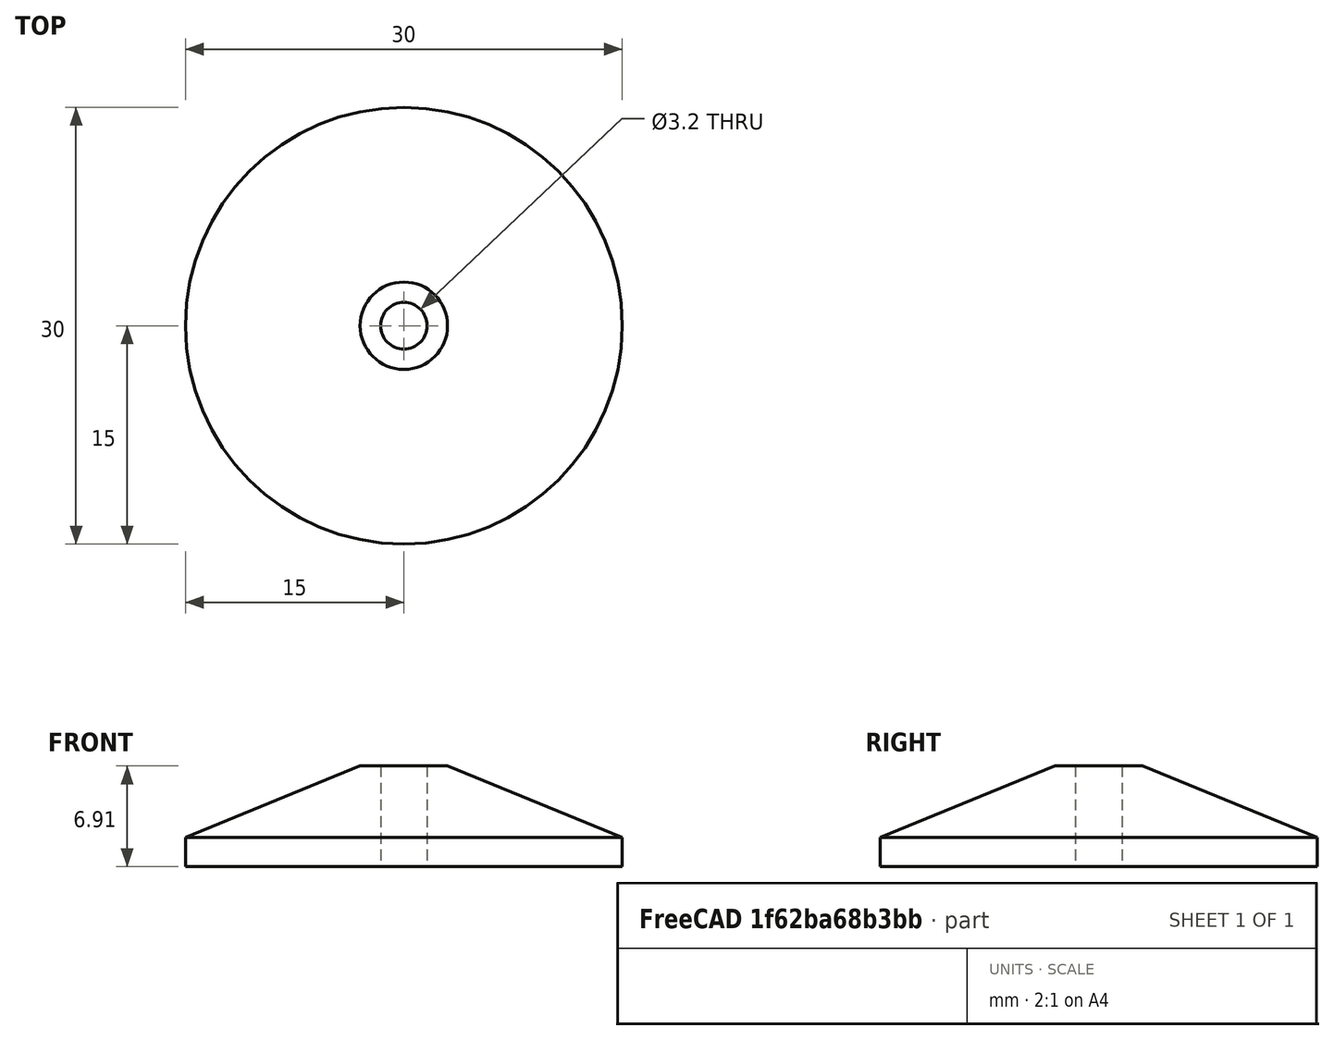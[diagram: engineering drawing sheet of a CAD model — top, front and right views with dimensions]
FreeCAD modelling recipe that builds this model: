
FCSTD DOCUMENT  (FreeCAD 0.21R33668 +26 (Git))
Label: BobbinSocket_Small_R_A2
License: All rights reserved
LicenseURL: http://en.wikipedia.org/wiki/All_rights_reserved
objects: Sketcher::SketchObject×1, PartDesign::Revolution×1, PartDesign::Body×1, App::Part×1
note: 4 computed .brp shape members not serialized (recipe doc carries the construction recipe); baked Part::Feature solids carry a one-line shape summary decoded from their .brp

FEATURE [Sketcher::SketchObject] Sketch002
  FullyConstrained = false
  MapMode = 5
  Placement = pos=(0,0,0) rot=(0.57735,0.57735,0.57735;2.0944rad)
  Support = -> [YZ_Plane001]
  sketch-geometry (5):
    g0: LineSegment StartX=1.6 StartY=6.90933 StartZ=0 EndX=1.6 EndY=0 EndZ=0
    g1: LineSegment StartX=15 StartY=0 StartZ=0 EndX=15 EndY=2 EndZ=0
    g2: LineSegment StartX=1.6 StartY=0 StartZ=0 EndX=15 EndY=0 EndZ=0
    g3: LineSegment StartX=1.6 StartY=6.90933 StartZ=0 EndX=3 EndY=6.90933 EndZ=0
    g4: LineSegment StartX=3 StartY=6.90933 StartZ=0 EndX=15 EndY=2 EndZ=0
  constraints (15):
    c: PointOnObject(g1,g-1)
    c: Vertical(g1)
    c: DistanceX(g-1,g0) = 1.6
    c: Vertical(g0)
    c: PointOnObject(g2,g-1)
    c: Coincident(g2,g1)
    c: DistanceX(g-1,g1) = 15
    c: Coincident(g0,g3)
    c: Horizontal(g3)
    c: Coincident(g3,g4)
    c: Coincident(g4,g1)
    c: DistanceX(g-1,g3) = 3
    c: Angle(g4,g2) = 0.388336
    c: Coincident(g2,g0)
    c: DistanceY(g1,g1) = 2
FEATURE [PartDesign::Revolution] Revolution
  AllowMultiFace = false
  Angle = 360
  Axis = (0,0,1)
  Base = (0,0,0)
  Placement = pos=(0,0,0) rot=(0.57735,0.57735,0.57735;2.0944rad)
  Profile = -> Sketch002
  ReferenceAxis = -> Sketch002 [V_Axis]
  Reversed = true
FEATURE [PartDesign::Body] RevolutionBody
  Group = -> [Sketch002,Revolution]
  Origin = -> Origin001
  Tip = -> Revolution
FEATURE [App::Part] Part
  Group = -> [RevolutionBody]
  License = CC BY 3.0
  LicenseURL = http://creativecommons.org/licenses/by/3.0/
  Origin = -> Origin
